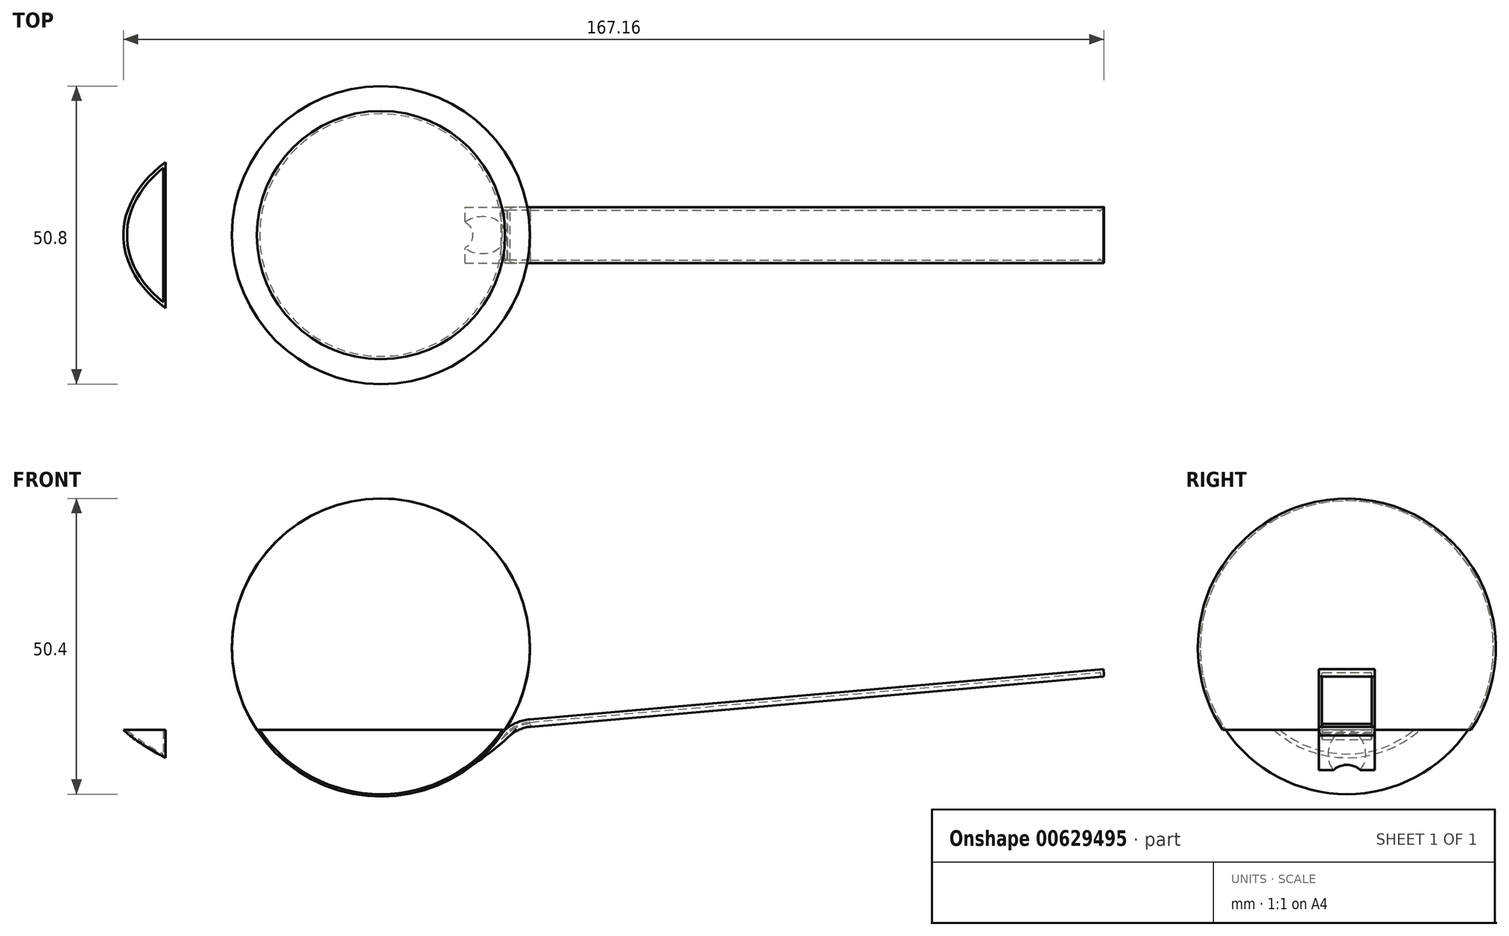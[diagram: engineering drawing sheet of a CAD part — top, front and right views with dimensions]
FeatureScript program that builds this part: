
annotation { "Feature Type Name" : "Feature", "Feature Type Description" : "" }
export const myFeature = defineFeature(function(context is Context, id is Id, definition is map)
    precondition{}
    {
        {
            var Q0;
            Q0=qCreatedBy(makeId("Top.planeOp"),FACE);
            var sketch = newSketch(context, id + "F0", { "sketchPlane" : qUnion([Q0])});
            skLineSegment(sketch, "E0.bottom", {"start": v(-25.32, 25.4) * mm, "end": v(-76.2, 25.4) * mm});
            skLineSegment(sketch, "E0.top", {"start": v(-25.48, -25.4) * mm, "end": v(-76.2, -25.4) * mm});
            skLineSegment(sketch, "E0.right", {"start": v(-76.2, 25.4) * mm, "end": v(-76.2, -25.4) * mm});
            skLineSegment(sketch, "E1", {"start": v(-76.2, 0) * mm, "end": v(-25.4, 0) * mm});
            skLineSegment(sketch, "E2", {"start": v(-62.1, -25.4) * mm, "end": v(-62.1, 25.4) * mm});
            skFitSpline(sketch, "E3", {"points": [v(-25.32, 25.4) * mm, v(-76.2, 0) * mm, v(-25.48, -25.4) * mm], "startDerivative": vector(-220.55, 0) * mm, "endDerivative": vector(219.85, 0) * mm});
            skLineSegment(sketch, "E4", {"start": v(-76.2, 0) * mm, "end": v(0, 0) * mm});
            skCircle(sketch, "E5", {"center": v(-25.4, 0) * mm, "radius": 25.4 * mm});
            skSolve(sketch);
        }
        {
            var Q0;
            {var subQ0=sQuery(id+"F0.wireOp",EDGE,"E3");var subQ1=sQuery(id+"F0.wireOp",EDGE,"E2");var subQ2=makeQuery(id+"F0.imprint","INTERSECT",VERTEX,{"disambiguationData":[OD(0.0)],"derivedFrom":[subQ1,subQ0]});Q0=makeQuery(id+"F0.imprint","IMPRINT",FACE,{"disambiguationData":[TD([[makeQuery(id+"F0.imprint","IMPRINT",EDGE,{"disambiguationData":[TD([[subQ2,-1.0]])],"derivedFrom":subQ1}),1.0]])]});}
            var Q1;
            {var subQ0=sQuery(id+"F0.wireOp",EDGE,"E3");var subQ1=sQuery(id+"F0.wireOp",EDGE,"E2");var subQ2=makeQuery(id+"F0.imprint","INTERSECT",VERTEX,{"disambiguationData":[OD(0.0)],"derivedFrom":[subQ1,subQ0]});Q1=makeQuery(id+"F0.imprint","IMPRINT",FACE,{"disambiguationData":[TD([[makeQuery(id+"F0.imprint","IMPRINT",EDGE,{"disambiguationData":[TD([[subQ2,-1.0]])],"derivedFrom":subQ1}),-1.0]])]});}
            var Q2;
            {var subQ0=sQuery(id+"F0.wireOp",EDGE,"E4");var subQ1=makeQuery(id+"F0.imprint","IMPRINT",VERTEX,{"derivedFrom":subQ0});Q2=makeQuery(id+"F0.imprint","IMPRINT",FACE,{"disambiguationData":[TD([[makeQuery(id+"F0.imprint","IMPRINT",EDGE,{"disambiguationData":[TD([[subQ1,1.0]])],"derivedFrom":subQ0}),-1.0]])]});}
            var Q3;
            Q3=sQuery(id+"F0.wireOp",EDGE,"E1");
            revolve(context, id + "F1", {"entities" : qUnion([Q0, Q1, Q2]), "axis" : qUnion([Q3]), "revolveType" : RevolveType.FULL});
        }
        {
            var Q0;
            Q0=qCreatedBy(makeId("Front.planeOp"),FACE);
            var sketch = newSketch(context, id + "F2", { "sketchPlane" : qUnion([Q0])});
            skLineSegment(sketch, "E6.bottom", {"start": v(3.17, 32.28) * mm, "end": v(-79.22, 32.28) * mm});
            skLineSegment(sketch, "E6.top", {"start": v(3.17, -14.06) * mm, "end": v(-79.22, -14.06) * mm});
            skLineSegment(sketch, "E6.left", {"start": v(3.17, 32.28) * mm, "end": v(3.17, -14.06) * mm});
            skLineSegment(sketch, "E6.right", {"start": v(-79.22, 32.28) * mm, "end": v(-79.22, -14.06) * mm});
            skSolve(sketch);
        }
        {
            var Q0;
            Q0 = qSketchRegion(id + "F2", true);
            extrude(context, id + "F3", {"entities" : qUnion([Q0]), "operationType" : NewBodyOperationType.REMOVE, "endBound" : BoundingType.SYMMETRIC, "oppositeDirection" : true, "depth" : 127 * mm, "offsetDistance" : 25.4 * mm});
        }
        {
            var Q0;
            Q0=makeQuery(id+"F3.boolean.opBoolean","COPY",FACE,{"derivedFrom":makeQuery(id+"F3.opExtrude","SWEPT_FACE",FACE,{"disambiguationData":[OSD([sQuery(id+"F2.wireOp",EDGE,"E6.top")])]})});
            shell(context, id + "F4", {"entities" : qUnion([Q0]), "thickness" : 0.4 * mm});
        }
        {
            var Q0;
            Q0=qCreatedBy(makeId("Front.planeOp"),FACE);
            var sketch = newSketch(context, id + "F5", { "sketchPlane" : qUnion([Q0])});
            skLineSegment(sketch, "E7.bottom", {"start": v(0, -12.24) * mm, "end": v(97.76, -3.68) * mm});
            skArc(sketch, "E8", {"start": v(0, -12.24) * mm, "mid": v(-2.27, -12.8) * mm, "end": v(-4.25, -14.06) * mm});
            skArc(sketch, "E9.0", {"start": v(0.11, -13.5) * mm, "mid": v(-1.77, -13.97) * mm, "end": v(-3.4, -15.01) * mm});
            skLineSegment(sketch, "E9.1", {"start": v(0.11, -13.5) * mm, "end": v(97.87, -4.95) * mm});
            skArc(sketch, "E10", {"start": v(-11.1, -20.87) * mm, "mid": v(-7.1, -18.13) * mm, "end": v(-3.4, -15.01) * mm});
            skArc(sketch, "E11", {"start": v(-11.1, -20.87) * mm, "mid": v(-7.45, -17.69) * mm, "end": v(-4.25, -14.06) * mm});
            skLineSegment(sketch, "E12", {"start": v(97.87, -4.95) * mm, "end": v(97.76, -3.68) * mm});
            skSolve(sketch);
        }
        {
            var Q0;
            Q0=makeQuery(id+"F5.imprint","IMPRINT",FACE,{"disambiguationData":[TD([[makeQuery(id+"F5.imprint","IMPRINT",EDGE,{"derivedFrom":sQuery(id+"F5.wireOp",EDGE,"E7.bottom")}),-1.0]])]});
            extrude(context, id + "F6", {"entities" : qUnion([Q0]), "operationType" : NewBodyOperationType.ADD, "endBound" : BoundingType.SYMMETRIC, "depth" : 9.52 * mm, "offsetDistance" : 25.4 * mm});
        }
        {
            var Q0;
            Q0=makeQuery(id+"F6.opExtrude","SWEPT_FACE",FACE,{"disambiguationData":[OSD([sQuery(id+"F5.wireOp",EDGE,"E9.1")])]});
            shell(context, id + "F7", {"entities" : qUnion([Q0]), "thickness" : 0.5 * mm});
        }
        {
            var Q0;
            Q0=makeQuery(id+"F7.opShell","OFFSET_FACE",FACE,{"disambiguationData":[OSD([sQuery(id+"F5.wireOp",EDGE,"E7.bottom")])]});
            var Q1;
            Q1=makeQuery(id+"F6.opExtrude","SWEPT_FACE",FACE,{"disambiguationData":[OSD([sQuery(id+"F5.wireOp",EDGE,"E9.1")])]});
            fillet(context, id + "F8", {"entities" : qUnion([Q0, Q1]), "radius" : 0.25 * mm, "tangentPropagation" : true, "allowEdgeOverflow" : false});
        }
    });
